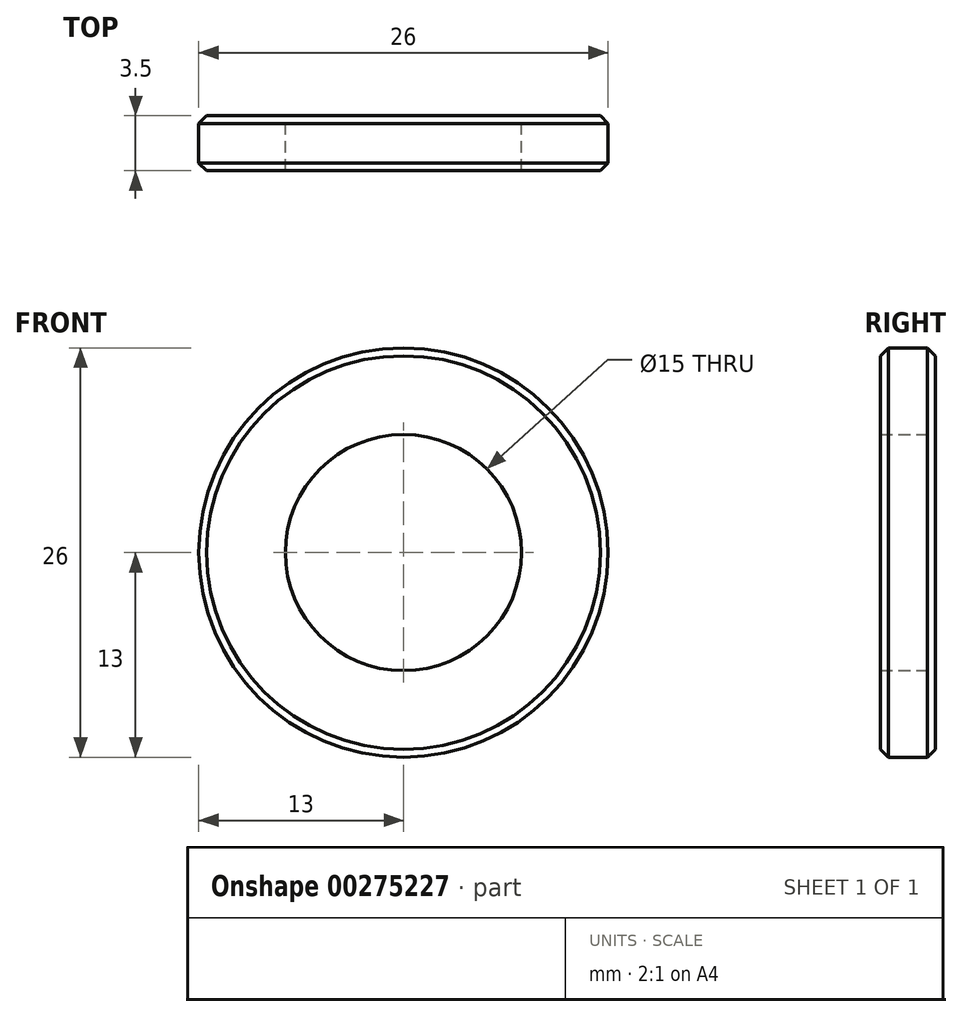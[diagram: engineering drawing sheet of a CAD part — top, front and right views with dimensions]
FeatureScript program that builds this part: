
annotation { "Feature Type Name" : "Feature", "Feature Type Description" : "" }
export const myFeature = defineFeature(function(context is Context, id is Id, definition is map)
    precondition{}
    {
        {
            var Q0;
            Q0=qCreatedBy(makeId("Front.planeOp"),FACE);
            var sketch = newSketch(context, id + "F0", { "sketchPlane" : qUnion([Q0])});
            skCircle(sketch, "E0", {"center": v(0, 0) * mm, "radius": 13 * mm});
            skCircle(sketch, "E1", {"center": v(0, 0) * mm, "radius": 7.5 * mm});
            skSolve(sketch);
        }
        {
            var Q0;
            Q0=makeQuery(id+"F0.imprint","IMPRINT",FACE,{"disambiguationData":[TD([[makeQuery(id+"F0.imprint","IMPRINT",EDGE,{"derivedFrom":sQuery(id+"F0.wireOp",EDGE,"E0")}),1.0]])]});
            extrude(context, id + "F1", {"entities" : qUnion([Q0]), "depth" : 3.5 * mm});
        }
        {
            var Q0;
            Q0=makeQuery(id+"F1.opExtrude","CAP_EDGE",EDGE,{"disambiguationData":[OSD([sQuery(id+"F0.wireOp",EDGE,"E0")])],"isStart":false});
            var Q1;
            Q1=makeQuery(id+"F1.opExtrude","CAP_EDGE",EDGE,{"disambiguationData":[OSD([sQuery(id+"F0.wireOp",EDGE,"E0")])],"isStart":true});
            chamfer(context, id + "F2", {"entities" : qUnion([Q0, Q1]), "chamferType" : ChamferType.OFFSET_ANGLE, "width" : .5 * mm, "oppositeDirection" : false, "angle" : 45 * degree, "tangentPropagation" : true});
        }
    });
